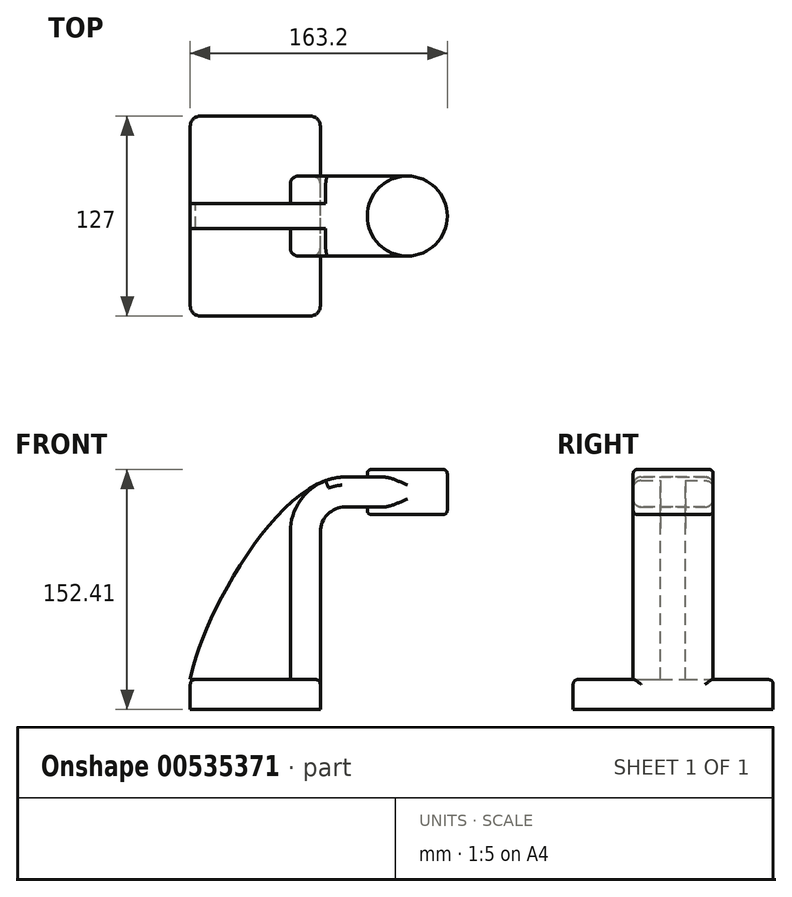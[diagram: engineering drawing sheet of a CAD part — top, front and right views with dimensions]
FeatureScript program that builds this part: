
annotation { "Feature Type Name" : "Feature", "Feature Type Description" : "" }
export const myFeature = defineFeature(function(context is Context, id is Id, definition is map)
    precondition{}
    {
        {
            var Q0;
            Q0=qCreatedBy(makeId("Front.planeOp"),FACE);
            var sketch = newSketch(context, id + "F0", { "sketchPlane" : qUnion([Q0])});
            skLineSegment(sketch, "E0.bottom", {"start": v(41.27, 9.52) * mm, "end": v(-41.28, 9.53) * mm});
            skLineSegment(sketch, "E0.top", {"start": v(41.28, -9.53) * mm, "end": v(-41.28, -9.52) * mm});
            skLineSegment(sketch, "E0.left", {"start": v(41.28, 9.52) * mm, "end": v(41.28, -9.53) * mm});
            skLineSegment(sketch, "E0.right", {"start": v(-41.28, 9.53) * mm, "end": v(-41.28, -9.52) * mm});
            skPoint(sketch, "E0.middle", {"position": v(0, 0) * mm});
            skLineSegment(sketch, "E1.bottom", {"start": v(121.92, 114.3) * mm, "end": v(71.12, 114.3) * mm});
            skLineSegment(sketch, "E1.top", {"start": v(121.92, 142.88) * mm, "end": v(71.12, 142.88) * mm});
            skLineSegment(sketch, "E1.left", {"start": v(121.92, 114.3) * mm, "end": v(121.92, 142.88) * mm});
            skLineSegment(sketch, "E1.right", {"start": v(71.12, 114.3) * mm, "end": v(71.12, 142.88) * mm});
            skPoint(sketch, "E1.middle", {"position": v(96.52, 128.59) * mm});
            skLineSegment(sketch, "E2", {"start": v(41.28, 9.52) * mm, "end": v(41.28, 103.2) * mm});
            skArc(sketch, "E3", {"start": v(41.28, 103.2) * mm, "mid": v(45.92, 114.43) * mm, "end": v(57.15, 119.08) * mm});
            skLineSegment(sketch, "E4", {"start": v(57.15, 119.08) * mm, "end": v(96.52, 119.08) * mm});
            skLineSegment(sketch, "E5.0", {"start": v(57.15, 138.13) * mm, "end": v(96.52, 138.13) * mm});
            skArc(sketch, "E5.1", {"start": v(22.23, 103.2) * mm, "mid": v(32.45, 127.9) * mm, "end": v(57.15, 138.13) * mm});
            skLineSegment(sketch, "E5.2", {"start": v(22.22, 9.52) * mm, "end": v(22.22, 103.2) * mm});
            skFitSpline(sketch, "E6", {"points": [v(-41.28, 9.53) * mm, v(57.15, 138.13) * mm], "startDerivative": vector(15.3, 100.98) * mm, "endDerivative": vector(133.2, -0.5) * mm});
            skLineSegment(sketch, "E7", {"start": v(96.52, 142.88) * mm, "end": v(96.52, 114.3) * mm});
            skSolve(sketch);
        }
        {
            var Q0;
            Q0=makeQuery(id+"F0.imprint","IMPRINT",FACE,{"disambiguationData":[TD([[makeQuery(id+"F0.imprint","IMPRINT",EDGE,{"derivedFrom":sQuery(id+"F0.wireOp",EDGE,"E0.top")}),-1.0]])]});
            extrude(context, id + "F1", {"entities" : qUnion([Q0]), "endBound" : BoundingType.SYMMETRIC, "depth" : 127 * mm, "offsetDistance" : 25.4 * mm});
        }
        {
            var Q0;
            {var subQ1=sQuery(id+"F0.wireOp",EDGE,"E2");Q0=makeQuery(id+"F0.imprint","IMPRINT",FACE,{"disambiguationData":[TD([[makeQuery(id+"F0.imprint","IMPRINT",EDGE,{"derivedFrom":subQ1}),1.0]])]});}
            var Q1;
            {var subQ0=sQuery(id+"F0.wireOp",EDGE,"E4");var subQ1=sQuery(id+"F0.wireOp",EDGE,"E1.right");var subQ2=makeQuery(id+"F0.imprint","INTERSECT",VERTEX,{"derivedFrom":[subQ1,subQ0]});Q1=makeQuery(id+"F0.imprint","IMPRINT",FACE,{"disambiguationData":[TD([[makeQuery(id+"F0.imprint","IMPRINT",EDGE,{"disambiguationData":[TD([[subQ2,-1.0]])],"derivedFrom":subQ1}),-1.0]])]});}
            extrude(context, id + "F2", {"entities" : qUnion([Q0, Q1]), "operationType" : NewBodyOperationType.ADD, "endBound" : BoundingType.SYMMETRIC, "depth" : 50.8 * mm, "offsetDistance" : 25.4 * mm});
        }
        {
            var Q0;
            {var subQ0=sQuery(id+"F0.wireOp",EDGE,"E1.left");Q0=makeQuery(id+"F0.imprint","IMPRINT",FACE,{"disambiguationData":[TD([[makeQuery(id+"F0.imprint","IMPRINT",EDGE,{"derivedFrom":subQ0}),1.0]])]});}
            var Q1;
            Q1=sQuery(id+"F0.wireOp",EDGE,"E7");
            revolve(context, id + "F3", {"operationType" : NewBodyOperationType.ADD, "entities" : qUnion([Q0]), "axis" : qUnion([Q1]), "revolveType" : RevolveType.FULL});
        }
        {
            var Q0;
            Q0=makeQuery(id+"F1.opExtrude","CAP_EDGE",EDGE,{"disambiguationData":[OSD([sQuery(id+"F0.wireOp",EDGE,"E0.right")])],"isStart":false});
            var Q1;
            Q1=makeQuery(id+"F1.opExtrude","CAP_EDGE",EDGE,{"disambiguationData":[OSD([sQuery(id+"F0.wireOp",EDGE,"E0.left")])],"isStart":false});
            var Q2;
            Q2=makeQuery(id+"F1.opExtrude","CAP_EDGE",EDGE,{"disambiguationData":[OSD([sQuery(id+"F0.wireOp",EDGE,"E0.right")])],"isStart":true});
            var Q3;
            Q3=makeQuery(id+"F1.opExtrude","CAP_EDGE",EDGE,{"disambiguationData":[OSD([sQuery(id+"F0.wireOp",EDGE,"E0.left")])],"isStart":true});
            fillet(context, id + "F4", {"entities" : qUnion([Q0, Q1, Q2, Q3]), "radius" : 6.35 * mm, "tangentPropagation" : true, "allowEdgeOverflow" : false});
        }
        {
            var Q0;
            Q0=makeQuery(id+"F0.imprint","IMPRINT",FACE,{"disambiguationData":[TD([[makeQuery(id+"F0.imprint","IMPRINT",EDGE,{"derivedFrom":sQuery(id+"F0.wireOp",EDGE,"E5.1")}),1.0]])]});
            extrude(context, id + "F5", {"entities" : qUnion([Q0]), "operationType" : NewBodyOperationType.ADD, "endBound" : BoundingType.SYMMETRIC, "depth" : 15.88 * mm, "offsetDistance" : 25.4 * mm});
        }
        {
            var Q0;
            Q0=makeQuery(id+"F5.opExtrude","CAP_EDGE",EDGE,{"disambiguationData":[OSD([sQuery(id+"F0.wireOp",EDGE,"E6")])],"isStart":true});
            var Q1;
            Q1=makeQuery(id+"F5.opExtrude","CAP_EDGE",EDGE,{"disambiguationData":[OSD([sQuery(id+"F0.wireOp",EDGE,"E6")])],"isStart":false});
            var Q2;
            Q2=makeQuery(id+"F2.opExtrude","CAP_EDGE",EDGE,{"disambiguationData":[OSD([sQuery(id+"F0.wireOp",EDGE,"E5.1")])],"isStart":true});
            var Q3;
            Q3=makeQuery(id+"F2.opExtrude","CAP_EDGE",EDGE,{"disambiguationData":[OSD([sQuery(id+"F0.wireOp",EDGE,"E5.2")])],"isStart":true});
            var Q4;
            Q4=makeQuery(id+"F2.opExtrude","CAP_EDGE",EDGE,{"disambiguationData":[OSD([sQuery(id+"F0.wireOp",EDGE,"E5.2")])],"isStart":false});
            var Q5;
            Q5=makeQuery(id+"F2.opExtrude","CAP_EDGE",EDGE,{"disambiguationData":[OSD([sQuery(id+"F0.wireOp",EDGE,"E5.1")])],"isStart":false});
            var Q6;
            Q6=makeQuery(id+"F2.opExtrude","CAP_EDGE",EDGE,{"disambiguationData":[OSD([sQuery(id+"F0.wireOp",EDGE,"E2")])],"isStart":true});
            var Q7;
            Q7=makeQuery(id+"F2.opExtrude","CAP_EDGE",EDGE,{"disambiguationData":[OSD([sQuery(id+"F0.wireOp",EDGE,"E3")])],"isStart":true});
            var Q8;
            Q8=makeQuery(id+"F2.opExtrude","CAP_EDGE",EDGE,{"disambiguationData":[OSD([sQuery(id+"F0.wireOp",EDGE,"E2")])],"isStart":false});
            var Q9;
            Q9=makeQuery(id+"F2.opExtrude","CAP_EDGE",EDGE,{"disambiguationData":[OSD([sQuery(id+"F0.wireOp",EDGE,"E3")])],"isStart":false});
            var Q10;
            Q10=makeQuery(id+"F2.opExtrude","CAP_EDGE",EDGE,{"disambiguationData":[OSD([sQuery(id+"F0.wireOp",EDGE,"E4")])],"isStart":false});
            var Q11;
            Q11=makeQuery(id+"F2.opExtrude","CAP_EDGE",EDGE,{"disambiguationData":[OSD([sQuery(id+"F0.wireOp",EDGE,"E4")])],"isStart":true});
            var Q12;
            Q12=makeQuery(id+"F2.opExtrude","CAP_EDGE",EDGE,{"disambiguationData":[OSD([sQuery(id+"F0.wireOp",EDGE,"E5.0")])],"isStart":true});
            var Q13;
            Q13=makeQuery(id+"F2.opExtrude","CAP_EDGE",EDGE,{"disambiguationData":[OSD([sQuery(id+"F0.wireOp",EDGE,"E5.0")])],"isStart":false});
            fillet(context, id + "F6", {"entities" : qUnion([Q0, Q1, Q2, Q3, Q4, Q5, Q6, Q7, Q8, Q9, Q10, Q11, Q12, Q13]), "radius" : 5.08 * mm, "tangentPropagation" : true, "allowEdgeOverflow" : false});
        }
        {
            var Q0;
            Q0=makeQuery(id+"F5.opExtrude","CAP_EDGE",EDGE,{"disambiguationData":[OSD([sQuery(id+"F0.wireOp",EDGE,"E5.1")])],"isStart":false});
            var Q1;
            Q1=makeQuery(id+"F5.opExtrude","CAP_EDGE",EDGE,{"disambiguationData":[OSD([sQuery(id+"F0.wireOp",EDGE,"E5.2")])],"isStart":false});
            var Q2;
            {var subQ0=sQuery(id+"F0.wireOp",EDGE,"E6");var subQ1=sQuery(id+"F0.wireOp",EDGE,"E0.bottom");var subQ2=sQuery(id+"F0.wireOp",EDGE,"E0.right");var subQ3=makeQuery(id+"F1.opExtrude","SWEPT_EDGE",EDGE,{"disambiguationData":[OSD([subQ1,subQ2,subQ0])]});Q2=makeQuery(id+"F6.opFillet","MERGE",EDGE,{"derivedFrom":[makeQuery(id+"F5.boolean.opBoolean","MERGE",EDGE,{"derivedFrom":[subQ3,makeQuery(id+"F5.opExtrude","SWEPT_EDGE",EDGE,{"disambiguationData":[OSD([subQ1,subQ2,subQ0])]})]}),makeQuery(id+"F5.boolean.opBoolean","SPLIT",EDGE,{"disambiguationData":[TD([makeQuery(id+"F4.opFillet","BLEND_FACE",FACE,{"disambiguationData":[OSD([subQ2]),TDD([makeQuery(id+"F1.opExtrude","CAP_EDGE",EDGE,{"disambiguationData":[OSD([subQ2])],"isStart":true})])]})])],"derivedFrom":subQ3})]});}
            var Q3;
            Q3=makeQuery(id+"F4.opFillet","BLEND_EDGE",EDGE,{"blendedFrom":[makeQuery(id+"F1.opExtrude","CAP_EDGE",EDGE,{"disambiguationData":[OSD([sQuery(id+"F0.wireOp",EDGE,"E0.right")])],"isStart":true}),makeQuery(id+"F1.opExtrude","SWEPT_FACE",FACE,{"disambiguationData":[OSD([sQuery(id+"F0.wireOp",EDGE,"E0.bottom")])]})],"blendedInto":[makeQuery(id+"F1.opExtrude","SWEPT_FACE",FACE,{"disambiguationData":[OSD([sQuery(id+"F0.wireOp",EDGE,"E0.bottom")])]})]});
            var Q4;
            Q4=makeQuery(id+"F1.opExtrude","CAP_EDGE",EDGE,{"disambiguationData":[OSD([sQuery(id+"F0.wireOp",EDGE,"E0.bottom")])],"isStart":true});
            var Q5;
            {var subQ0=sQuery(id+"F0.wireOp",EDGE,"E6");var subQ1=sQuery(id+"F0.wireOp",EDGE,"E0.bottom");var subQ2=sQuery(id+"F0.wireOp",EDGE,"E0.right");var subQ3=makeQuery(id+"F1.opExtrude","SWEPT_EDGE",EDGE,{"disambiguationData":[OSD([subQ1,subQ2,subQ0])]});Q5=makeQuery(id+"F6.opFillet","MERGE",EDGE,{"derivedFrom":[makeQuery(id+"F5.boolean.opBoolean","MERGE",EDGE,{"derivedFrom":[subQ3,makeQuery(id+"F5.opExtrude","SWEPT_EDGE",EDGE,{"disambiguationData":[OSD([subQ1,subQ2,subQ0])]})]}),makeQuery(id+"F5.boolean.opBoolean","SPLIT",EDGE,{"disambiguationData":[TD([makeQuery(id+"F4.opFillet","BLEND_FACE",FACE,{"disambiguationData":[OSD([subQ2]),TDD([makeQuery(id+"F1.opExtrude","CAP_EDGE",EDGE,{"disambiguationData":[OSD([subQ2])],"isStart":false})])]})])],"derivedFrom":subQ3})]});}
            var Q6;
            Q6=makeQuery(id+"F4.opFillet","BLEND_EDGE",EDGE,{"blendedFrom":[makeQuery(id+"F1.opExtrude","CAP_EDGE",EDGE,{"disambiguationData":[OSD([sQuery(id+"F0.wireOp",EDGE,"E0.right")])],"isStart":false}),makeQuery(id+"F1.opExtrude","SWEPT_FACE",FACE,{"disambiguationData":[OSD([sQuery(id+"F0.wireOp",EDGE,"E0.bottom")])]})],"blendedInto":[makeQuery(id+"F1.opExtrude","SWEPT_FACE",FACE,{"disambiguationData":[OSD([sQuery(id+"F0.wireOp",EDGE,"E0.bottom")])]})]});
            var Q7;
            Q7=makeQuery(id+"F1.opExtrude","CAP_EDGE",EDGE,{"disambiguationData":[OSD([sQuery(id+"F0.wireOp",EDGE,"E0.bottom")])],"isStart":false});
            fillet(context, id + "F7", {"entities" : qUnion([Q0, Q1, Q2, Q3, Q4, Q5, Q6, Q7]), "radius" : 3.17 * mm, "tangentPropagation" : true, "allowEdgeOverflow" : false});
        }
        {
            var Q0;
            Q0=makeQuery(id+"F3.opRevolve","SWEPT_EDGE",EDGE,{"disambiguationData":[OSD([sQuery(id+"F0.wireOp",EDGE,"E1.top"),sQuery(id+"F0.wireOp",EDGE,"E1.left")])]});
            var Q1;
            Q1=makeQuery(id+"F3.opRevolve","SWEPT_EDGE",EDGE,{"disambiguationData":[OSD([sQuery(id+"F0.wireOp",EDGE,"E1.bottom"),sQuery(id+"F0.wireOp",EDGE,"E1.left")])]});
            fillet(context, id + "F8", {"entities" : qUnion([Q0, Q1]), "radius" : 2.54 * mm, "tangentPropagation" : true, "allowEdgeOverflow" : false});
        }
        {
            var Q0;
            {var subQ3=sQuery(id+"F0.wireOp",EDGE,"E5.2");Q0=makeQuery(id+"F0.imprint","IMPRINT",FACE,{"disambiguationData":[TD([[makeQuery(id+"F0.imprint","IMPRINT",EDGE,{"derivedFrom":subQ3}),1.0]])]});}
            extrude(context, id + "F9", {"entities" : qUnion([Q0]), "operationType" : NewBodyOperationType.ADD, "endBound" : BoundingType.SYMMETRIC, "depth" : 15.88 * mm, "offsetDistance" : 25.4 * mm});
        }
    });
